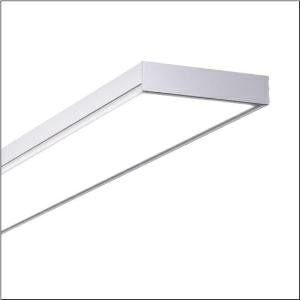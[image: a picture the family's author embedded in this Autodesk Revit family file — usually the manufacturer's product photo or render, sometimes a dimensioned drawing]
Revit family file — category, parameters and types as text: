
# Revit family: apollon_r__31_surface_51mp26wm2441e_3eed
name_source: partatom
category: Lighting Fixtures
units: mm (PartAtom-declared; Revit-internal decimal feet)

## family parameters
Cut with Voids When Loaded = No
Host = Face
Light Source = No
Part Type = Normal
Room Calculation Point = No
Round Connector Dimension = Use Diameter
Shared = No

## types (1)
- Apollon® 31 Surface (1 x LED, 4600 lm, 33 W, 4000K)
    Apparent Load = 33 VA
    CIE Flux Codes = 61 87 97 97 100
    Color Rendering = 80
    Color Temperature = 4000K
    Default Elevation = 1800 mm
    Description = Apollon® 31 Surface, office luminaire, primary optical cover: micro prismatic cover, of PMMA, light emission: direct distribution, primary light characteristic: symmetric, installation type: surface-mounted, LED, rated luminous flux: 4.600lm, luminous efficacy: 139lm/W, light colour: 840, colour temperature: 4000K, control gear: ECG Multilumen, with terminal, 3-pole, mains connection: 220..240V, AC, 50/60Hz, rated input power: 33W, housing, of sheet steel, coil coated, metallic grey (RAL 9006), length: 1.545mm, width: 200mm, height: 44mm, protection rating (complete): IP20, insulation class (complete): insulation class II (safety insulation), certification: CE, impact resistance: IK02, permissible operating ambient temperature: -20..+40°C, packaging unit: 1 piece
    Height = 44 mm
    Lamp = 1 x LED
    Lamp Light Flux = 4600 lm
    Lamp Power = 33 W
    Lamp count = 1
    Length = 1545 mm
    Luminous efficacy = 139 lm/W
    Manufacturer = Siteco
    ModVariant = No
    Model = 51MP26WM2441E
    Mounting Place = Ceiling
    Mounting Type = Surface mounted
    Number of Poles = 1
    OnlyDefault = Yes
    Power Factor = 1
    Product Name = Apollon® 31 Surface
    Product group = office luminaire | ceiling mounted
    ProductGroupID = 304
    Protection Class = Protection class II
    Protection Degree = IP 20
    RLX_Detail_Level = 1
    RLX_Emergency_Light_Flux = 0 lm
    RLX_Emergency_Type = 0
    RLX_Emergency_Type_DB = No
    RlxData = <blob elided: 24089 chars, md5=0390f77e>
    Socket = socket
    Standby Power = 0 W
    System Light Flux = 4600 lm
    System Power = 33 W
    Type Comments = Product without accessories
    Type Image = l_1007091.jpg
    URL = http://relux.com
    VarID = ---
    Voltage = 0 V
    Weight = 0.00 kg
    Width = 200 mm  [stored 0.656168 ft]

note: [stored X ft] marks values corroborated as IEEE doubles in the binary element streams (Revit-internal decimal feet)

## geometry (parser evidence)
native form markers: Blend x4, Sweep x10
no freeform markers — native parametric forms only
